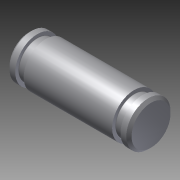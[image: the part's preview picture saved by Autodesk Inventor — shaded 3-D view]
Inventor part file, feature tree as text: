
AUTODESK INVENTOR PART (.ipt)
format: ipt  version: 2012 (Build 160160000, 160)  size: 139,776 bytes
history: native  units: in
note: dims shown in document units (in); Inventor stores cm internally (conversion verified against a paired STEP export)
features: other x49, revolve x1, sketch x1
ambient origin geometry x8: Origin, YZ Plane, XZ Plane, XY Plane, X Axis, Y Axis, Z Axis, Center Point
bodies: Solid1 (feature_tree)
feature tree (51):
  revolve  "Revolution1"  [1 undecoded]
  other  "pin_XY"
  other  "pin_YZ"
  other  "pin_ZX"
  other  "pin_X"
  other  "pin_Y"
  other  "pin_Z"
  other  "pin_Center"
  other  "rr1_XY"
  other  "rr1_YZ"
  other  "rr1_ZX"
  other  "rr1_X"
  other  "rr1_Y"
  other  "rr1_Z"
  other  "rr1_Center"
  other  "rr2_XY"
  other  "rr2_YZ"
  other  "rr2_ZX"
  other  "rr2_X"
  other  "rr2_Y"
  other  "rr2_Z"
  other  "rr2_Center"
  other  "w21_XY"
  other  "w21_YZ"
  other  "w21_ZX"
  other  "w21_X"
  other  "w21_Y"
  other  "w21_Z"
  other  "w21_Center"
  other  "w22_XY"
  other  "w22_YZ"
  other  "w22_ZX"
  other  "w22_X"
  other  "w22_Y"
  other  "w22_Z"
  other  "w22_Center"
  other  "p1_XY"
  other  "p1_YZ"
  other  "p1_ZX"
  other  "p1_X"
  other  "p1_Y"
  other  "p1_Z"
  other  "p1_Center"
  other  "p2_XY"
  other  "p2_YZ"
  other  "p2_ZX"
  other  "p2_X"
  other  "p2_Y"
  other  "p2_Z"
  other  "p2_Center"
  sketch  "Sketch_1"  dims[d0=360.0deg]
note: 1 required parameter value undecoded (feature->parameter linkage not recoverable at this tier; creation-order binding heuristic only, values carry confidence <= 0.55)
